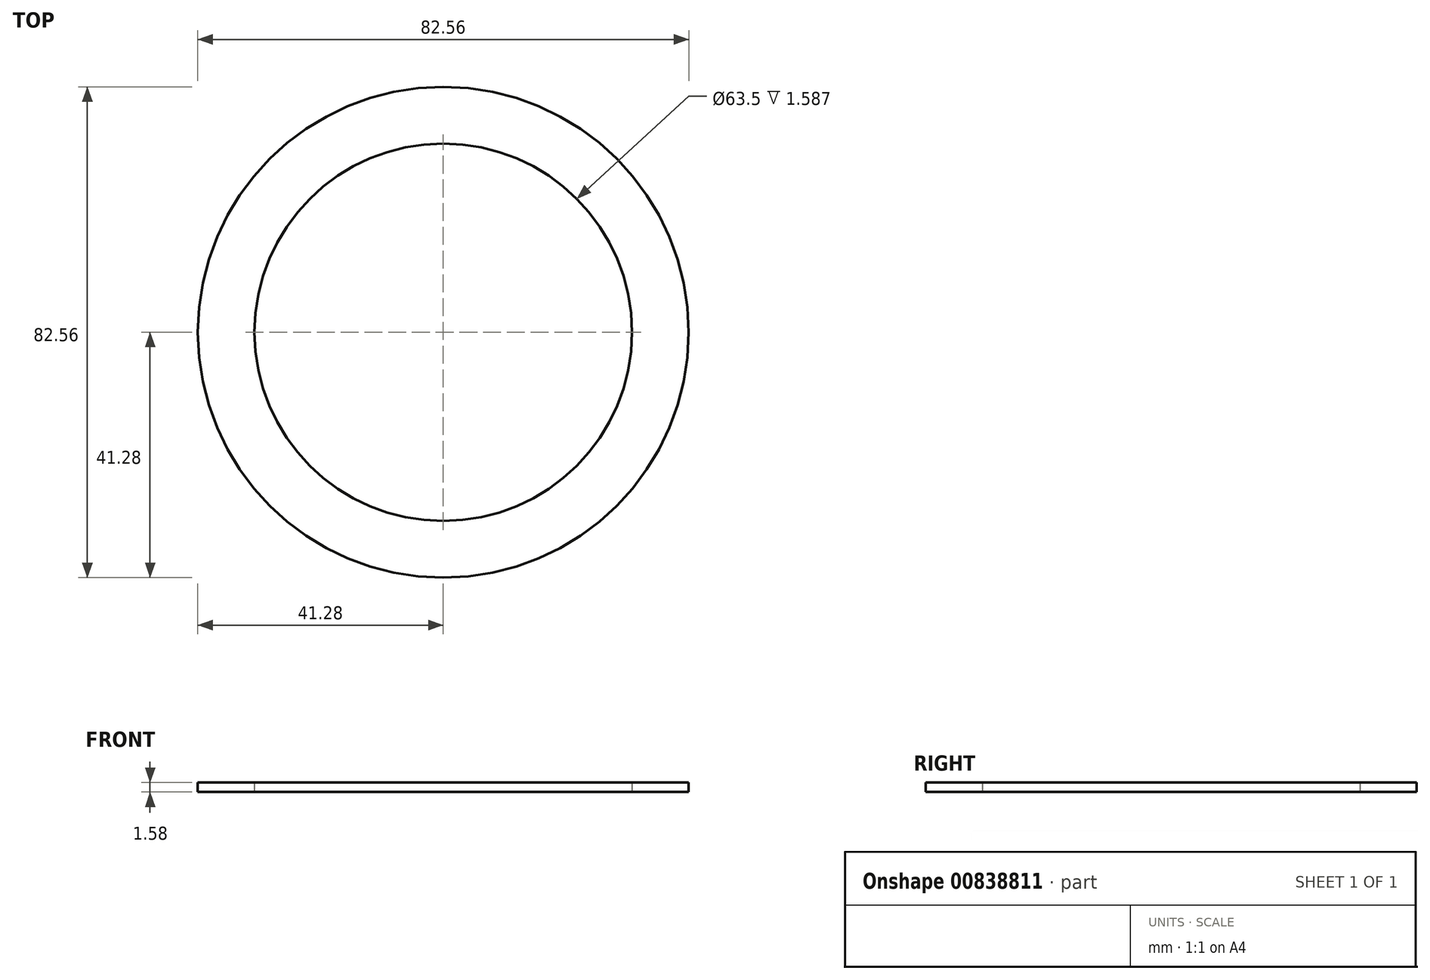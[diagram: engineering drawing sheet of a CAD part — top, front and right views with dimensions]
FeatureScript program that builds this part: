
annotation { "Feature Type Name" : "Feature", "Feature Type Description" : "" }
export const myFeature = defineFeature(function(context is Context, id is Id, definition is map)
    precondition{}
    {
        {
            var Q0;
            Q0=qCreatedBy(makeId("Top.planeOp"),FACE);
            var sketch = newSketch(context, id + "F0", { "sketchPlane" : qUnion([Q0])});
            skCircle(sketch, "E0", {"center": v(0, 0) * mm, "radius": 31.75 * mm});
            skCircle(sketch, "E1", {"center": v(0, 0) * mm, "radius": 41.28 * mm});
            skSolve(sketch);
        }
        {
            var Q0;
            Q0=qSketchRegion(id+"F0",true);
            extrude(context, id + "F1", {"entities" : qUnion([Q0]), "endBound" : BoundingType.SYMMETRIC, "depth" : 1.59 * mm, "offsetDistance" : 25.4 * mm});
        }
    });
